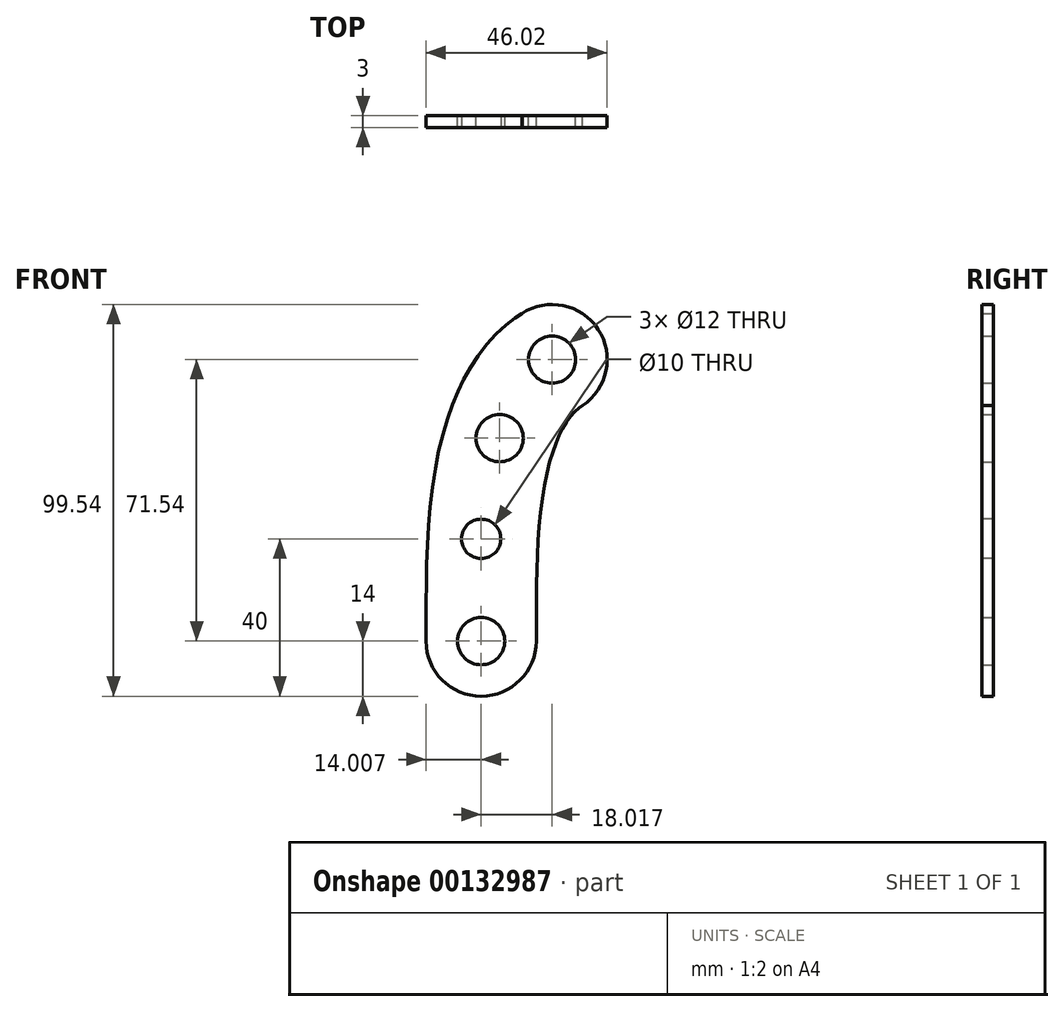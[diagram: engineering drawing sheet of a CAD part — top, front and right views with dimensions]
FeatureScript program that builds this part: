
annotation { "Feature Type Name" : "Feature", "Feature Type Description" : "" }
export const myFeature = defineFeature(function(context is Context, id is Id, definition is map)
    precondition{}
    {
        {
            var Q0;
            Q0=qCreatedBy(makeId("Front.planeOp"),FACE);
            var sketch = newSketch(context, id + "F0", { "sketchPlane" : qUnion([Q0])});
            skCircle(sketch, "E0", {"center": v(18.02, 45.54) * mm, "radius": 6 * mm});
            skCircle(sketch, "E1", {"center": v(4.7, 25.57) * mm, "radius": 6 * mm});
            skCircle(sketch, "E2", {"center": v(0, -26) * mm, "radius": 6 * mm});
            skFitSpline(sketch, "E3", {"points": [v(0, -26) * mm, v(18.02, 45.54) * mm], "startDerivative": vector(0, 78) * mm, "endDerivative": vector(54.05, 35.54) * mm, "construction": true});
            skLineSegment(sketch, "E4.0", {"start": v(-8.67, 29.71) * mm, "end": v(-8.67, 29.71) * mm});
            skArc(sketch, "E5.0", {"start": v(-14, -26) * mm, "mid": v(0, -40) * mm, "end": v(14, -26) * mm});
            skFitSpline(sketch, "E6.0", {"points": [v(14, -26) * mm, v(14, -22.75) * mm, v(14, -16.1) * mm, v(14.2, -6.04) * mm, v(14.8, 3.77) * mm, v(15.94, 12.9) * mm, v(17.44, 19.57) * mm, v(18.94, 24.08) * mm, v(20.19, 27) * mm, v(21.52, 29.42) * mm, v(22.9, 31.34) * mm, v(24.28, 32.8) * mm, v(25.22, 33.52) * mm, v(25.7, 33.84) * mm]});
            skFitSpline(sketch, "E7.0", {"points": [v(-14, -26) * mm, v(-14, -22.75) * mm, v(-14, -15.91) * mm, v(-13.78, -5) * mm, v(-13.11, 6.2) * mm, v(-11.72, 17.47) * mm, v(-9.7, 26.7) * mm, v(-7.32, 33.89) * mm, v(-5.09, 39.15) * mm, v(-2.31, 44.24) * mm, v(1.12, 49.07) * mm, v(5.28, 53.5) * mm, v(8.56, 56.08) * mm, v(10.32, 57.24) * mm]});
            skArc(sketch, "E8.trimOffspring", {"start": v(25.7, 33.84) * mm, "mid": v(29.71, 53.23) * mm, "end": v(10.32, 57.24) * mm});
            skLineSegment(sketch, "E9.trimOffspring", {"start": v(18.08, 21.43) * mm, "end": v(18.08, 21.43) * mm});
            skPoint(sketch, "E10", {"position": v(-13.46, 0) * mm});
            skSolve(sketch);
        }
        {
            var Q0;
            Q0=makeQuery(id+"F0.imprint","IMPRINT",FACE,{"disambiguationData":[TD([[makeQuery(id+"F0.imprint","IMPRINT",EDGE,{"derivedFrom":sQuery(id+"F0.wireOp",EDGE,"E0")}),-1.0]])]});
            extrude(context, id + "F1", {"entities" : qUnion([Q0]), "depth" : 3 * mm});
        }
        {
            var Q0;
            Q0=makeQuery(id+"F1.opExtrude","SWEPT_BODY",BODY,{"disambiguationData":[OSD([sQuery(id+"F0.wireOp",EDGE,"Sjf7detk-OeFK-TYrE-BgNc-QToHNdDsGX7T"),sQuery(id+"F0.wireOp",EDGE,"E0"),sQuery(id+"F0.wireOp",EDGE,"E1"),sQuery(id+"F0.wireOp",EDGE,"E2"),sQuery(id+"F0.wireOp",EDGE,"E5.0"),sQuery(id+"F0.wireOp",EDGE,"E6.0"),sQuery(id+"F0.wireOp",EDGE,"E7.0"),sQuery(id+"F0.wireOp",EDGE,"E8.trimOffspring")])]});
            transform(context, id + "F2", {"entities" : qUnion([Q0]), "transformType" : TransformType.TRANSLATION_3D, "dx" : 50.9 * mm, "dy" : 0 * mm, "dz" : 0 * mm, "makeCopy" : true});
        }
        {
            var Q0;
            Q0=makeQuery(id+"F2.opPattern","COPY",FACE,{"derivedFrom":makeQuery(id+"F1.opExtrude","CAP_FACE",FACE,{"disambiguationData":[OSD([sQuery(id+"F0.wireOp",EDGE,"E0"),sQuery(id+"F0.wireOp",EDGE,"E1"),sQuery(id+"F0.wireOp",EDGE,"E2"),sQuery(id+"F0.wireOp",EDGE,"E5.0"),sQuery(id+"F0.wireOp",EDGE,"E6.0"),sQuery(id+"F0.wireOp",EDGE,"E7.0"),sQuery(id+"F0.wireOp",EDGE,"E8.trimOffspring")])],"isStart":false}),"instanceName":"1"});
            var sketch = newSketch(context, id + "F3", { "sketchPlane" : qUnion([Q0])});
            skCircle(sketch, "E11", {"center": v(50.9, 0) * mm, "radius": 5 * mm});
            skPoint(sketch, "E12", {"position": v(37.44, 0) * mm});
            skSolve(sketch);
        }
        {
            var Q0;
            Q0=makeQuery(id+"F3.imprint","IMPRINT",FACE,{"disambiguationData":[TD([[makeQuery(id+"F3.imprint","IMPRINT",EDGE,{"derivedFrom":sQuery(id+"F3.wireOp",EDGE,"E11")}),1.0]])]});
            extrude(context, id + "F4", {"entities" : qUnion([Q0]), "operationType" : NewBodyOperationType.REMOVE, "oppositeDirection" : true, "offsetDistance" : 25 * mm, "depth" : 9.4 * mm});
        }
        {
            var Q0;
            Q0=makeQuery(id+"F1.opExtrude","CAP_FACE",FACE,{"disambiguationData":[OSD([sQuery(id+"F0.wireOp",EDGE,"E0"),sQuery(id+"F0.wireOp",EDGE,"E1"),sQuery(id+"F0.wireOp",EDGE,"E2"),sQuery(id+"F0.wireOp",EDGE,"E5.0"),sQuery(id+"F0.wireOp",EDGE,"E6.0"),sQuery(id+"F0.wireOp",EDGE,"E7.0"),sQuery(id+"F0.wireOp",EDGE,"E8.trimOffspring")])],"isStart":true});
            var sketch = newSketch(context, id + "F5", { "sketchPlane" : qUnion([Q0])});
            skCircle(sketch, "E13", {"center": v(0, 0) * mm, "radius": 5 * mm});
            skSolve(sketch);
        }
        {
            var Q0;
            Q0=makeQuery(id+"F5.imprint","IMPRINT",FACE,{"disambiguationData":[TD([[makeQuery(id+"F5.imprint","IMPRINT",EDGE,{"derivedFrom":sQuery(id+"F5.wireOp",EDGE,"E13")}),1.0]])]});
            extrude(context, id + "F6", {"entities" : qUnion([Q0]), "operationType" : NewBodyOperationType.REMOVE, "oppositeDirection" : true, "depth" : 2 * mm});
        }
        {
            var Q0;
            Q0=makeQuery(id+"F1.opExtrude","SWEPT_BODY",BODY,{"disambiguationData":[OSD([sQuery(id+"F0.wireOp",EDGE,"E0"),sQuery(id+"F0.wireOp",EDGE,"E1"),sQuery(id+"F0.wireOp",EDGE,"E2"),sQuery(id+"F0.wireOp",EDGE,"E5.0"),sQuery(id+"F0.wireOp",EDGE,"E6.0"),sQuery(id+"F0.wireOp",EDGE,"E7.0"),sQuery(id+"F0.wireOp",EDGE,"E8.trimOffspring")])]});
            deleteBodies(context, id + "F7", {"entities" : qUnion([Q0])});
        }
    });
